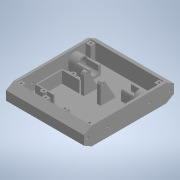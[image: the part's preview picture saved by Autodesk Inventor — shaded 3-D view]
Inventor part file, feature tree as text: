
AUTODESK INVENTOR PART (.ipt)
format: ipt  version: 2020 (Build 240168000, 168)  size: 488,448 bytes
history: native  units: in
note: dims shown in document units (in); Inventor stores cm internally (conversion verified against a paired STEP export)
features: extrude x14, sketch x14, projected_geometry x14, mirror x4, plane x2
ambient origin geometry x8: Origin, YZ Plane, XZ Plane, XY Plane, X Axis, Y Axis, Z Axis, Center Point
bodies: Solid1 (feature_tree)
feature tree (48):
  extrude  "Extrusion1"  Depth=5.9055in
  extrude  "Extrusion2"  TaperAngle=0.0deg  [1 undecoded]
  extrude  "Extrusion3"  Depth=1.063in
  extrude  "Extrusion4"  Depth=0.315in
  extrude  "Extrusion5"  TaperAngle=0.0deg  [1 undecoded]
  extrude  "Extrusion6"  Depth=0.5906in
  mirror  "Mirror1"
  extrude  "Extrusion7"  Depth=0.0787in
  mirror  "Mirror2"
  extrude  "Extrusion8"  Depth=0.6102in
  mirror  "Mirror3"
  plane  "Work Plane1"
  extrude  "Extrusion9"  Depth=0.7874in TaperAngle=0.0deg
  mirror  "Mirror4"
  extrude  "Extrusion10"  Depth=6.063in TaperAngle=0.0deg
  extrude  "Extrusion11"  Depth=0.1575in
  extrude  "Extrusion12"  TaperAngle=0.0deg  [1 undecoded]
  extrude  "Extrusion13"  Depth=0.2756in
  extrude  "Extrusion14"  Depth=0.4331in
  plane  "Work Plane2"
  sketch  "Sketch1"  dims[d0=1.1811in d1=5.9055in]
  sketch  "Sketch2"  dims[d2=5.1181in d3=0.0in]
  projected_geometry  "Projected Loop1"
  sketch  "Sketch3"  dims[d4=0.1575in d5=1.063in]
  projected_geometry  "Projected Loop2"
  projected_geometry  "Projected Loop3"
  sketch  "Sketch4"  dims[d6=0.0in d8=0.315in]
  sketch  "Sketch5"  dims[d10=0.993in d11=0.0in]
  projected_geometry  "Projected Loop4"
  sketch  "Sketch6"  dims[d12=0.6496in d13=0.5906in]
  sketch  "Sketch7"  dims[d14=1.5748in d15=0.0787in]
  sketch  "Sketch9"  dims[d16=0.5512in d17=0.0in d18=0.6102in]
  sketch  "Sketch10"  dims[d19=0.4803in d20=0.7874in d21=0.0in]
  sketch  "Sketch12"  dims[d22=0.1654in d23=6.063in d24=0.0in]
  projected_geometry  "Projected Loop6"
  projected_geometry  "Projected Loop7"
  projected_geometry  "Projected Loop8"
  sketch  "Sketch13"  dims[d25=0.5114in d26=0.1575in]
  projected_geometry  "Projected Loop9"
  projected_geometry  "Projected Loop10"
  projected_geometry  "Projected Loop11"
  projected_geometry  "Projected Loop12"
  projected_geometry  "Projected Loop13"
  projected_geometry  "Projected Loop14"
  sketch  "Sketch14"  dims[d27=1.5748in d28=0.0in d29=0.0in]
  sketch  "Sketch15"  dims[d30=0.1575in d31=0.2756in]
  projected_geometry  "Projected Loop15"
  sketch  "Sketch16"  dims[d32=0.0in d33=0.4331in d34=0.122in d38=2.7559in d40=0.061in d41=0.0909in d42=0.2362in d43=0.0in d44=60.0deg d45=0.0787in d46=0.315in d48=0.993in d49=0.0in d51=0.1476in d53=0.2756in d54=0.0in d55=0.4724in d56=1.2008in d57=1.6142in d58=1.5945in d59=0.0787in d60=0.0787in d62=0.315in d63=0.7677in d64=0.0in d66=0.1476in d67=0.2756in d68=0.0in d69=0.8268in d70=0.2953in d71=0.0394in d72=0.0in]
note: 3 required parameter values undecoded (feature->parameter linkage not recoverable at this tier; creation-order binding heuristic only, values carry confidence <= 0.55)
